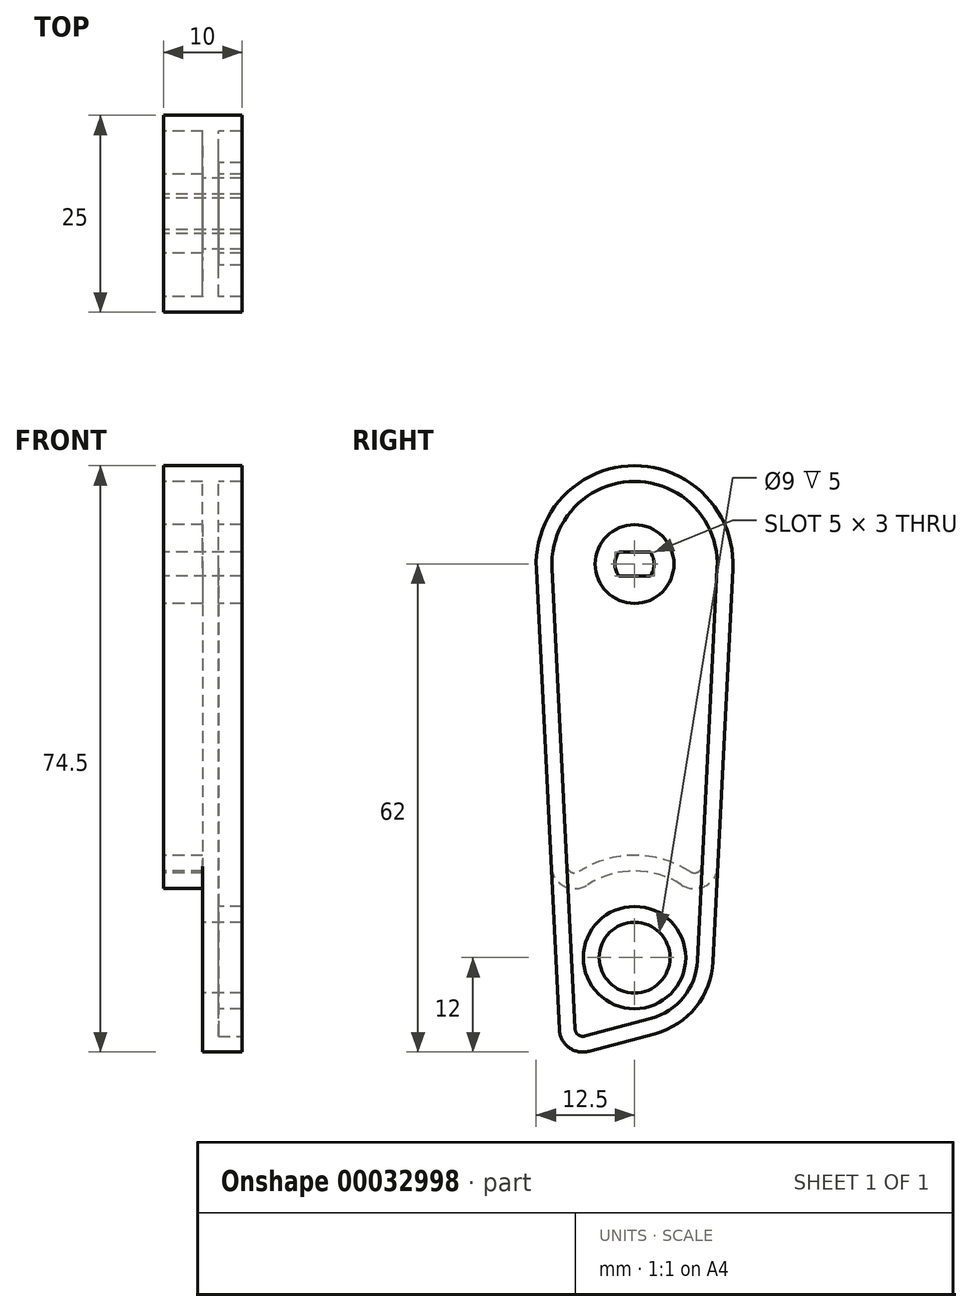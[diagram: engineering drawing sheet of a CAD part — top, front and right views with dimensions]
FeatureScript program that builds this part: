
annotation { "Feature Type Name" : "Feature", "Feature Type Description" : "" }
export const myFeature = defineFeature(function(context is Context, id is Id, definition is map)
    precondition{}
    {
        {
            var Q0;
            Q0=qCreatedBy(makeId("Right.planeOp"),FACE);
            var sketch = newSketch(context, id + "F0", { "sketchPlane" : qUnion([Q0])});
            skArc(sketch, "E0", {"start": v(12.48, -0.63) * mm, "mid": v(0, 12.5) * mm, "end": v(-12.48, -0.62) * mm});
            skArc(sketch, "E1", {"start": v(2.59, -59.66) * mm, "mid": v(7.78, -56.28) * mm, "end": v(9.99, -50.5) * mm});
            skLineSegment(sketch, "E2", {"start": v(-12.48, -0.62) * mm, "end": v(-9.37, -62.86) * mm});
            skLineSegment(sketch, "E3", {"start": v(-9.37, -62.86) * mm, "end": v(2.59, -59.66) * mm});
            skLineSegment(sketch, "E4", {"start": v(9.99, -50.5) * mm, "end": v(12.48, -0.62) * mm});
            skLineSegment(sketch, "E5", {"start": v(0, -50) * mm, "end": v(0, 0) * mm, "construction": true});
            skSolve(sketch);
        }
        {
            var Q0;
            Q0 = qSketchRegion(id + "F0", true);
            extrude(context, id + "F1", {"entities" : qUnion([Q0]), "depth" : 10 * mm});
        }
        {
            var Q0;
            Q0=qCreatedBy(makeId("Right.planeOp"),FACE);
            var sketch = newSketch(context, id + "F2", { "sketchPlane" : qUnion([Q0])});
            skArc(sketch, "E6.0", {"start": v(2.59, -59.66) * mm, "mid": v(7.78, -56.28) * mm, "end": v(9.99, -50.5) * mm, "construction": true});
            skCircle(sketch, "E7", {"center": v(0, -50) * mm, "radius": 11 * mm, "construction": true});
            skArc(sketch, "E8", {"start": v(-11, -50) * mm, "mid": v(0, -39) * mm, "end": v(11, -50) * mm});
            skLineSegment(sketch, "E9", {"start": v(-11, -50) * mm, "end": v(-11, -80) * mm});
            skLineSegment(sketch, "E10", {"start": v(-11, -80) * mm, "end": v(11, -80) * mm});
            skLineSegment(sketch, "E11", {"start": v(11, -80) * mm, "end": v(11, -50) * mm});
            skLineSegment(sketch, "E12", {"start": v(-11, -50) * mm, "end": v(11, -50) * mm, "construction": true});
            skSolve(sketch);
        }
        {
            var Q0;
            Q0 = qSketchRegion(id + "F2", true);
            extrude(context, id + "F3", {"entities" : qUnion([Q0]), "operationType" : NewBodyOperationType.REMOVE, "depth" : 5 * mm});
        }
        {
            var Q0;
            Q0=qCreatedBy(makeId("Right.planeOp"),FACE);
            var sketch = newSketch(context, id + "F4", { "sketchPlane" : qUnion([Q0])});
            skArc(sketch, "E13.0", {"start": v(2.59, -59.66) * mm, "mid": v(7.78, -56.28) * mm, "end": v(9.99, -50.5) * mm, "construction": true});
            skCircle(sketch, "E14", {"center": v(0, -50) * mm, "radius": 4.5 * mm});
            skSolve(sketch);
        }
        {
            var Q0;
            Q0 = qSketchRegion(id + "F4", true);
            extrude(context, id + "F5", {"entities" : qUnion([Q0]), "operationType" : NewBodyOperationType.REMOVE, "endBound" : BoundingType.THROUGH_ALL, "depth" : 25 * mm});
        }
        {
            var Q0;
            Q0=makeQuery(id+"F1.opExtrude","CAP_FACE",FACE,{"disambiguationData":[OSD([sQuery(id+"F0.wireOp",EDGE,"E0"),sQuery(id+"F0.wireOp",EDGE,"E1"),sQuery(id+"F0.wireOp",EDGE,"E2"),sQuery(id+"F0.wireOp",EDGE,"E3"),sQuery(id+"F0.wireOp",EDGE,"E4")])],"isStart":true});
            var Q1;
            Q1=makeQuery(id+"F1.opExtrude","CAP_FACE",FACE,{"disambiguationData":[OSD([sQuery(id+"F0.wireOp",EDGE,"E0"),sQuery(id+"F0.wireOp",EDGE,"E1"),sQuery(id+"F0.wireOp",EDGE,"E2"),sQuery(id+"F0.wireOp",EDGE,"E3"),sQuery(id+"F0.wireOp",EDGE,"E4")])],"isStart":false});
            shell(context, id + "F6", {"entities" : qUnion([Q0, Q1]), "thickness" : 2 * mm});
        }
        {
            var Q0;
            Q0=makeQuery(id+"F6.opShell","OFFSET_EDGE",EDGE,{"disambiguationData":[OSD([sQuery(id+"F0.wireOp",EDGE,"E4"),sQuery(id+"F2.wireOp",EDGE,"E8")])]});
            var Q1;
            Q1=makeQuery(id+"F6.opShell","OFFSET_EDGE",EDGE,{"disambiguationData":[OSD([sQuery(id+"F0.wireOp",EDGE,"E2"),sQuery(id+"F2.wireOp",EDGE,"E8")])]});
            var Q2;
            Q2=makeQuery(id+"F6.opShell","OFFSET_EDGE",EDGE,{"disambiguationData":[OSD([sQuery(id+"F0.wireOp",EDGE,"E2"),sQuery(id+"F0.wireOp",EDGE,"E3")])]});
            fillet(context, id + "F7", {"entities" : qUnion([Q0, Q1, Q2]), "radius" : 1 * mm, "tangentPropagation" : true, "allowEdgeOverflow" : false});
        }
        {
            var Q0;
            Q0=makeQuery(id+"F3.boolean.opBoolean","INTERSECT",EDGE,{"derivedFrom":[makeQuery(id+"F1.opExtrude","SWEPT_FACE",FACE,{"disambiguationData":[OSD([sQuery(id+"F0.wireOp",EDGE,"E4")])]}),makeQuery(id+"F3.opExtrude","SWEPT_FACE",FACE,{"disambiguationData":[OSD([sQuery(id+"F2.wireOp",EDGE,"E8")])]})]});
            var Q1;
            Q1=makeQuery(id+"F3.boolean.opBoolean","INTERSECT",EDGE,{"derivedFrom":[makeQuery(id+"F1.opExtrude","SWEPT_FACE",FACE,{"disambiguationData":[OSD([sQuery(id+"F0.wireOp",EDGE,"E2")])]}),makeQuery(id+"F3.opExtrude","SWEPT_FACE",FACE,{"disambiguationData":[OSD([sQuery(id+"F2.wireOp",EDGE,"E8")])]})]});
            var Q2;
            Q2=makeQuery(id+"F1.opExtrude","SWEPT_EDGE",EDGE,{"disambiguationData":[OSD([sQuery(id+"F0.wireOp",EDGE,"E2"),sQuery(id+"F0.wireOp",EDGE,"E3")])]});
            fillet(context, id + "F8", {"entities" : qUnion([Q0, Q1, Q2]), "radius" : 3 * mm, "tangentPropagation" : true, "allowEdgeOverflow" : false});
        }
        {
            var Q0;
            Q0=makeQuery(id+"F3.boolean.opBoolean","COPY",FACE,{"derivedFrom":makeQuery(id+"F3.opExtrude","CAP_FACE",FACE,{"disambiguationData":[OSD([sQuery(id+"F2.wireOp",EDGE,"E8"),sQuery(id+"F2.wireOp",EDGE,"E9"),sQuery(id+"F2.wireOp",EDGE,"E10"),sQuery(id+"F2.wireOp",EDGE,"E11")])],"isStart":false})});
            var sketch = newSketch(context, id + "F9", { "sketchPlane" : qUnion([Q0])});
            skArc(sketch, "E15.0", {"start": v(-8.6, -38.3) * mm, "mid": v(-8.05, -39.13) * mm, "end": v(-7.05, -39.08) * mm});
            skArc(sketch, "E15.1", {"start": v(7.05, -39.08) * mm, "mid": v(0, -37) * mm, "end": v(-7.05, -39.08) * mm});
            skArc(sketch, "E15.2", {"start": v(7.05, -39.08) * mm, "mid": v(8.05, -39.13) * mm, "end": v(8.6, -38.3) * mm});
            skLineSegment(sketch, "E16", {"start": v(-8.6, -38.3) * mm, "end": v(-10.49, -0.53) * mm});
            skLineSegment(sketch, "E17", {"start": v(10.49, -0.52) * mm, "end": v(8.6, -38.3) * mm});
            skArc(sketch, "E18", {"start": v(-10.49, -0.53) * mm, "mid": v(0, 10.5) * mm, "end": v(10.49, -0.52) * mm});
            skSolve(sketch);
        }
        {
            var Q0;
            Q0 = qSketchRegion(id + "F9", true);
            extrude(context, id + "F10", {"entities" : qUnion([Q0]), "operationType" : NewBodyOperationType.ADD, "oppositeDirection" : true, "depth" : 2 * mm});
        }
        {
            var Q0;
            Q0=qCreatedBy(makeId("Right.planeOp"),FACE);
            var sketch = newSketch(context, id + "F11", { "sketchPlane" : qUnion([Q0])});
            skCircle(sketch, "E19", {"center": v(0, 0) * mm, "radius": 5 * mm});
            skSolve(sketch);
        }
        {
            var Q0;
            Q0 = qSketchRegion(id + "F11", true);
            extrude(context, id + "F12", {"entities" : qUnion([Q0]), "operationType" : NewBodyOperationType.ADD, "depth" : 10 * mm});
        }
        {
            var Q0;
            Q0=qCreatedBy(makeId("Right.planeOp"),FACE);
            var sketch = newSketch(context, id + "F13", { "sketchPlane" : qUnion([Q0])});
            skArc(sketch, "E20", {"start": v(2, -1.5) * mm, "mid": v(2.5, 0) * mm, "end": v(2, 1.5) * mm});
            skLineSegment(sketch, "E21", {"start": v(-2, 1.5) * mm, "end": v(2, 1.5) * mm});
            skLineSegment(sketch, "E22", {"start": v(2, -1.5) * mm, "end": v(-2, -1.5) * mm});
            skArc(sketch, "E23.trimOffspring", {"start": v(-2, 1.5) * mm, "mid": v(-2.5, 0) * mm, "end": v(-2, -1.5) * mm});
            skSolve(sketch);
        }
        {
            var Q0;
            Q0 = qSketchRegion(id + "F13", true);
            extrude(context, id + "F14", {"entities" : qUnion([Q0]), "operationType" : NewBodyOperationType.REMOVE, "endBound" : BoundingType.THROUGH_ALL, "depth" : 25 * mm});
        }
    });
